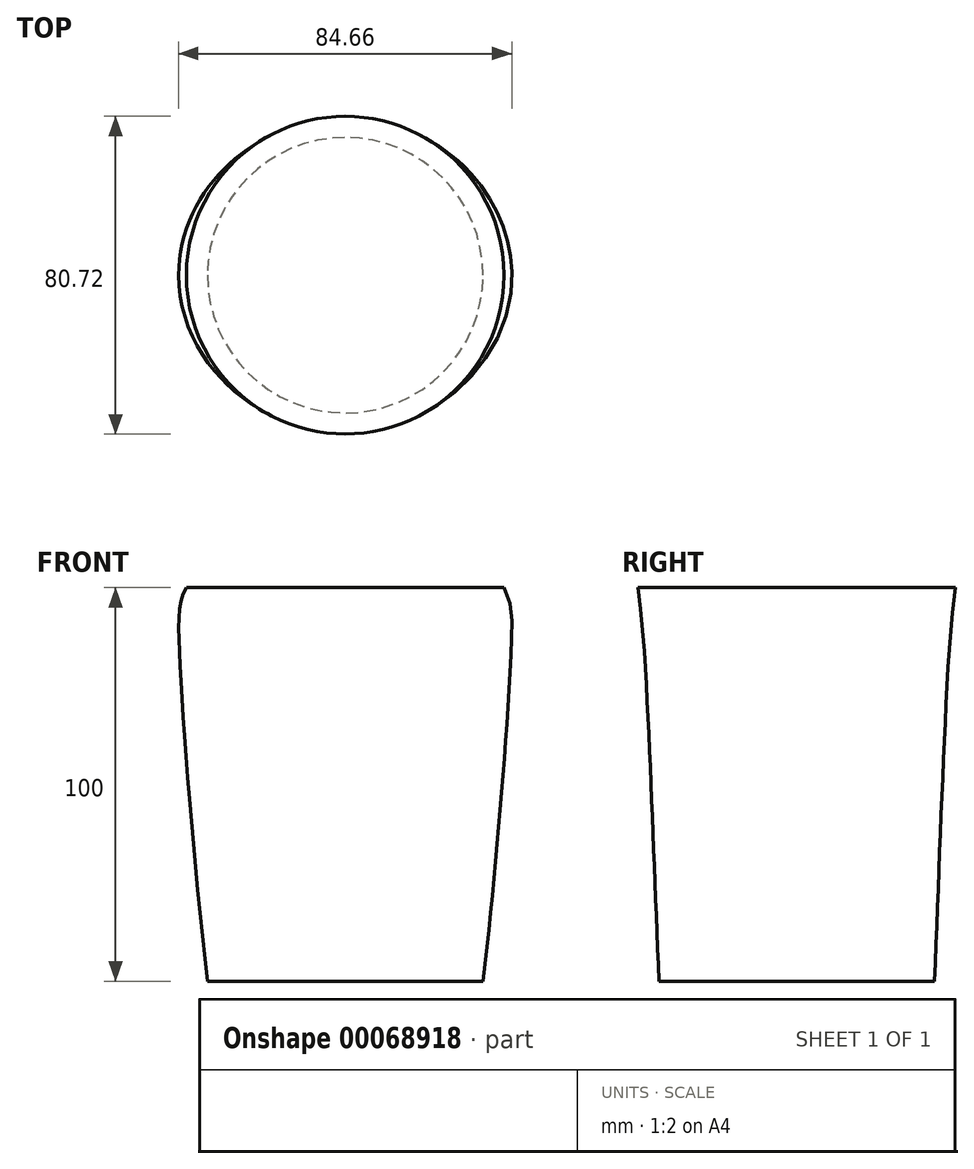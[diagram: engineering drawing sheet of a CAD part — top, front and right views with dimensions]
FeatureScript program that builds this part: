
annotation { "Feature Type Name" : "Feature", "Feature Type Description" : "" }
export const myFeature = defineFeature(function(context is Context, id is Id, definition is map)
    precondition{}
    {
        {
            var Q0;
            Q0=qCreatedBy(makeId("Top.planeOp"),FACE);
            var sketch = newSketch(context, id + "F0", { "sketchPlane" : qUnion([Q0])});
            skCircle(sketch, "E0", {"center": v(0, 0) * mm, "radius": 35 * mm});
            skLineSegment(sketch, "E1", {"start": v(0, 0) * mm, "end": v(-35, 0) * mm, "construction": true});
            skSolve(sketch);
        }
        {
            var Q0;
            Q0=qCreatedBy(makeId("Top.planeOp"),FACE);
            cPlane(context, id + "F1", {"entities" : qUnion([Q0]), "cplaneType" : CPlaneType.OFFSET, "offset" : 100 * mm, "width" : 150 * mm, "height" : 150 * mm});
        }
        {
            var Q0;
            Q0=qCreatedBy(id+"F1.planeOp",FACE);
            var sketch = newSketch(context, id + "F2", { "sketchPlane" : qUnion([Q0])});
            skCircle(sketch, "E2", {"center": v(0, 0) * mm, "radius": 40.36 * mm});
            skLineSegment(sketch, "E3", {"start": v(0, 0) * mm, "end": v(-40.36, 0) * mm, "construction": true});
            skSolve(sketch);
        }
        {
            var Q0;
            Q0=qCreatedBy(makeId("Front.planeOp"),FACE);
            var sketch = newSketch(context, id + "F3", { "sketchPlane" : qUnion([Q0])});
            skFitSpline(sketch, "E4", {"points": [v(-35, 0) * mm, v(-42.13, 83.3) * mm, v(-40.36, 100) * mm], "startDerivative": vector(-15.33, 129.28) * mm, "endDerivative": vector(21.15, 36.22) * mm});
            skFitSpline(sketch, "E5.MirrorCS", {"points": [v(35, 0) * mm, v(42.13, 83.3) * mm, v(40.36, 100) * mm], "startDerivative": vector(15.33, 129.28) * mm, "endDerivative": vector(-21.15, 36.22) * mm});
            skSolve(sketch);
        }
        {
            var Q0;
            Q0=makeQuery(id+"F2.imprint","IMPRINT",FACE,{"disambiguationData":[TD([[makeQuery(id+"F2.imprint","IMPRINT",EDGE,{"derivedFrom":sQuery(id+"F2.wireOp",EDGE,"E2")}),1.0]])]});
            var Q1;
            Q1=makeQuery(id+"F0.imprint","IMPRINT",FACE,{"disambiguationData":[TD([[makeQuery(id+"F0.imprint","IMPRINT",EDGE,{"derivedFrom":sQuery(id+"F0.wireOp",EDGE,"E0")}),1.0]])]});
            var Q2;
            Q2=sQuery(id+"F3.wireOp",EDGE,"E4");
            var Q3;
            Q3=sQuery(id+"F3.wireOp",EDGE,"E5.MirrorCS");
            loft(context, id + "F4", {"addGuides" : true, "sheetProfilesArray" : [{ "sheetProfileEntities" : qUnion([Q0]) }, { "sheetProfileEntities" : qUnion([Q1]) }], "guidesArray" : [{ "guideEntities" : qUnion([Q2]), "guideDerivativeType" : LoftGuideDerivativeType.DEFAULT, "guideDerivativeMagnitude" : 1 }, { "guideEntities" : qUnion([Q3]), "guideDerivativeType" : LoftGuideDerivativeType.DEFAULT, "guideDerivativeMagnitude" : 1 }]});
        }
    });
